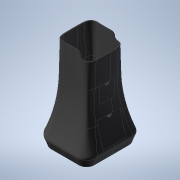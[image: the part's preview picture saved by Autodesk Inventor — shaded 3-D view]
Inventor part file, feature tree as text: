
AUTODESK INVENTOR PART (.ipt)
format: ipt  version: 2021 (Build 250183000, 183)  size: 5,649,920 bytes
history: native  units: mm
features: other x59, sketch x34, plane x22, hole x20, projected_geometry x17, extrude x7, fillet x3, loft x1, shell x1, mirror x1
ambient origin geometry x8: Origin, YZ Plane, XZ Plane, XY Plane, X Axis, Y Axis, Z Axis, Center Point
bodies: Body1 (feature_tree), Body2 (feature_tree), Body3 (feature_tree), Body4 (feature_tree), Body5 (feature_tree), Body6 (feature_tree), Body7 (feature_tree), Body8 (feature_tree), Body9 (feature_tree), Body10 (feature_tree), Body11 (feature_tree), Body12 (feature_tree), Body13 (feature_tree), Body14 (feature_tree), Body15 (feature_tree), Body16 (feature_tree), Body17 (feature_tree)
feature tree (165):
  other  "實體1"
  extrude  "擠出1"  Depth=284.5mm
  plane  "工作平面1"
  sketch  "草圖2"
  plane  "工作平面8"
  sketch  "草圖10"
  plane  "工作平面9"
  sketch  "草圖12"
  plane  "工作平面10"
  sketch  "草圖13"
  plane  "工作平面11"
  sketch  "草圖14"
  plane  "工作平面12"
  sketch  "草圖15"
  plane  "工作平面13"
  sketch  "草圖16"
  plane  "工作平面14"
  sketch  "草圖17"
  plane  "工作平面15"
  loft  "斷面混成1"
  shell  "薄殼1"  Thickness=50.0mm
  hole  "孔1"  [1 undecoded]
  plane  "工作平面16"
  other  "分割1"
  hole  "孔2"  [1 undecoded]
  hole  "孔3"  [1 undecoded]
  extrude  "擠出3"  Depth=225.0mm
  fillet  "圓角1"  Radius=50.0mm
  extrude  "擠出4"  Depth=400.0mm
  hole  "孔6"  [1 undecoded]
  extrude  "擠出6"  Depth=10.0mm
  fillet  "圓角2"  Radius=25.0mm
  plane  "工作平面17"
  plane  "工作平面29"
  plane  "工作平面30"
  other  "凸轂4"
  plane  "工作平面31"
  other  "凸轂5"
  mirror  "鏡射13"
  other  "分割4"
  other  "直接編輯1"
  extrude  "擠出36"  Depth=400.0mm
  fillet  "圓角4"  Radius=800.0mm
  plane  "工作平面34"
  plane  "工作平面35"
  plane  "工作平面36"
  plane  "工作平面37"
  other  "分割5"
  other  "分割6"
  other  "分割7"
  other  "分割8"
  other  "分割9"
  plane  "工作平面38"
  plane  "工作平面39"
  other  "分割10"
  other  "分割11"
  other  "分割12"
  other  "分割13"
  other  "分割14"
  other  "分割15"
  sketch  "草圖104"
  hole  "孔29"  [1 undecoded]
  hole  "孔30"  [1 undecoded]
  sketch  "草圖105"
  hole  "孔31"  [1 undecoded]
  hole  "孔32"  [1 undecoded]
  sketch  "草圖106"
  hole  "孔33"  [1 undecoded]
  hole  "孔34"  [1 undecoded]
  sketch  "草圖107"
  hole  "孔35"  [1 undecoded]
  hole  "孔36"  [1 undecoded]
  sketch  "草圖108"
  hole  "孔37"  [1 undecoded]
  hole  "孔38"  [1 undecoded]
  sketch  "草圖109"
  hole  "孔39"  [1 undecoded]
  hole  "孔40"  [1 undecoded]
  sketch  "草圖110"
  hole  "孔41"  [1 undecoded]
  hole  "孔42"  [1 undecoded]
  sketch  "草圖111"
  hole  "孔43"  [1 undecoded]
  hole  "孔44"  [1 undecoded]
  extrude  "擠出38"  Depth=25.0mm
  extrude  "擠出39"  Depth=800.0mm
  plane  "工作平面41"
  other  "凸轂6"
  sketch  "草圖1"
  sketch  "草圖18"
  sketch  "草圖19"
  sketch  "草圖20"
  other  "Srf2"
  sketch  "草圖21"
  projected_geometry  "投影迴路3"
  sketch  "草圖22"
  projected_geometry  "投影迴路4"
  sketch  "草圖24"
  projected_geometry  "投影迴路10"
  sketch  "草圖25"
  projected_geometry  "投影迴路11"
  sketch  "草圖29"
  projected_geometry  "投影迴路14"
  sketch  "草圖30"
  sketch  "草圖86"
  other  "Srf5"
  sketch  "草圖87"
  sketch  "草圖88"
  sketch  "草圖93"
  other  "Srf6"
  sketch  "草圖94"
  projected_geometry  "投影迴路75"
  projected_geometry  "投影迴路80"
  projected_geometry  "投影迴路81"
  projected_geometry  "投影迴路82"
  projected_geometry  "投影迴路83"
  projected_geometry  "投影迴路84"
  projected_geometry  "投影迴路85"
  projected_geometry  "投影迴路86"
  projected_geometry  "投影迴路87"
  sketch  "草圖112"
  projected_geometry  "投影迴路88"
  sketch  "草圖113"
  projected_geometry  "投影迴路89"
  plane  "工作平面40"
  sketch  "草圖114"
  projected_geometry  "投影迴路90"
  other  "擠出表面2"
  other  "擠出表面5"
  other  "擠出表面6"
  other  "投影切割邊5"
  other  "投影切割邊7"
  other  "投影切割邊8"
  other  "投影切割邊9"
  other  "投影切割邊10"
  other  "投影切割邊11"
  other  "投影切割邊12"
  other  "投影切割邊13"
  other  "實體2"
  other  "實體3"
  other  "實體12"
  other  "實體13"
  other  "移動1"
  other  "實體14"
  other  "實體15"
  other  "實體16"
  other  "實體17"
  other  "實體18"
  other  "實體19"
  other  "實體20"
  other  "實體21"
  other  "實體22"
  other  "實體23"
  other  "實體24"
  other  "實體25"
  other  "實體26"
  other  "實體27"
  other  "實體28"
  other  "實體29"
  other  "實體30"
  other  "實體31"
  other  "實體32"
  other  "實體33"
  other  "實體34"
  other  "實體35"
note: 20 required parameter values undecoded (feature->parameter linkage not recoverable at this tier; creation-order binding heuristic only, values carry confidence <= 0.55)
